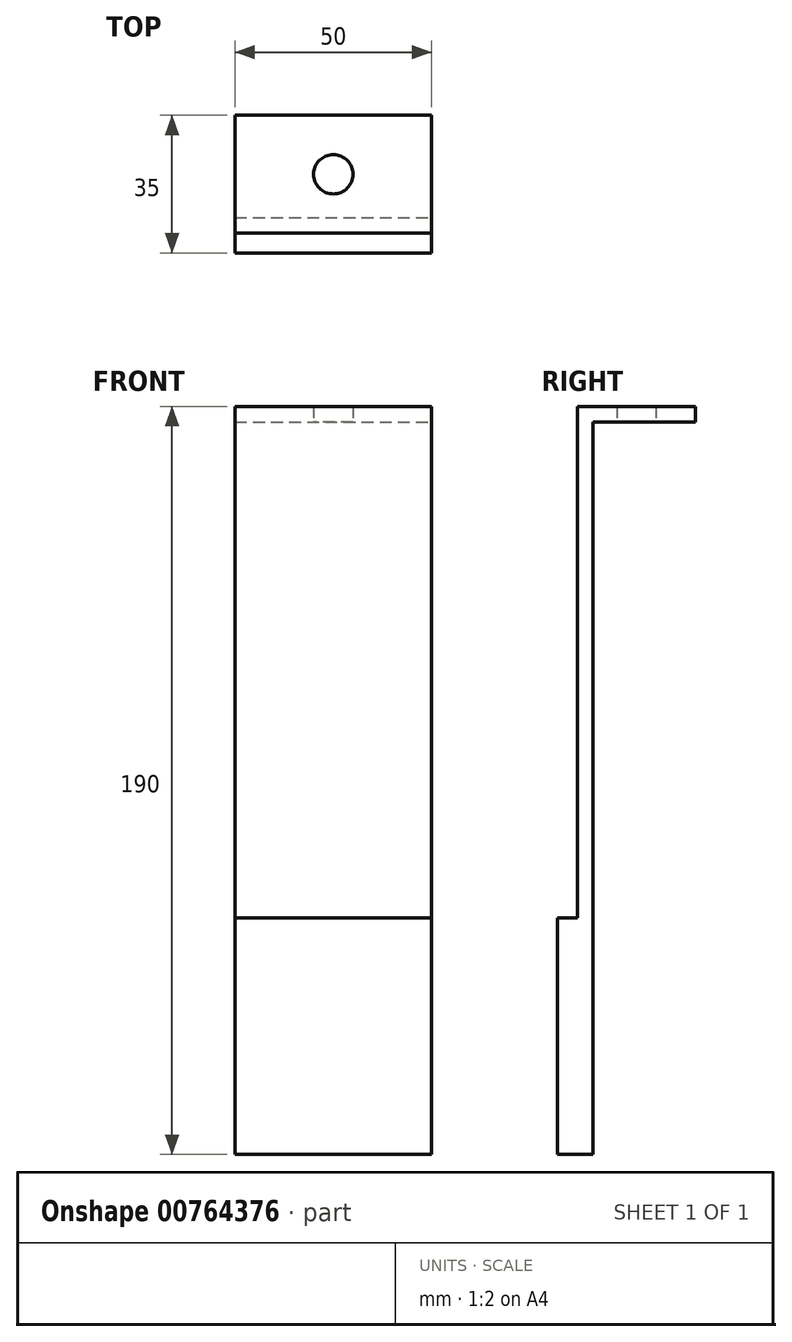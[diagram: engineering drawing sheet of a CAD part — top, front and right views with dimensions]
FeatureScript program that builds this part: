
annotation { "Feature Type Name" : "Feature", "Feature Type Description" : "" }
export const myFeature = defineFeature(function(context is Context, id is Id, definition is map)
    precondition{}
    {
        {
            var Q0;
            Q0=qCreatedBy(makeId("Front.planeOp"),FACE);
            var sketch = newSketch(context, id + "F0", { "sketchPlane" : qUnion([Q0])});
            skLineSegment(sketch, "E0.bottom", {"start": v(-24.82, -95) * mm, "end": v(25.18, -95) * mm});
            skLineSegment(sketch, "E0.top", {"start": v(-24.82, 91) * mm, "end": v(25.18, 91) * mm});
            skLineSegment(sketch, "E0.left", {"start": v(-24.82, -95) * mm, "end": v(-24.82, 91) * mm});
            skLineSegment(sketch, "E0.right", {"start": v(25.18, -95) * mm, "end": v(25.18, 91) * mm});
            skSolve(sketch);
        }
        {
            var Q0;
            Q0=makeQuery(id+"F0.imprint","IMPRINT",FACE,{"disambiguationData":[TD([[makeQuery(id+"F0.imprint","IMPRINT",EDGE,{"derivedFrom":sQuery(id+"F0.wireOp",EDGE,"E0.bottom")}),1.0]])]});
            extrude(context, id + "F1", {"entities" : qUnion([Q0]), "depth" : 4 * mm, "offsetDistance" : 25 * mm, "symmetric" : true});
        }
        {
            var Q0;
            Q0=makeQuery(id+"F1.opExtrude","SWEPT_FACE",FACE,{"disambiguationData":[OSD([sQuery(id+"F0.wireOp",EDGE,"E0.top")])]});
            var sketch = newSketch(context, id + "F2", { "sketchPlane" : qUnion([Q0])});
            skLineSegment(sketch, "E1.bottom", {"start": v(-24.82, -2) * mm, "end": v(25.18, -2) * mm});
            skLineSegment(sketch, "E1.top", {"start": v(-24.82, 28) * mm, "end": v(25.18, 28) * mm});
            skLineSegment(sketch, "E1.left", {"start": v(-24.82, -2) * mm, "end": v(-24.82, 28) * mm});
            skLineSegment(sketch, "E1.right", {"start": v(25.18, -2) * mm, "end": v(25.18, 28) * mm});
            skCircle(sketch, "E2", {"center": v(0.18, 13) * mm, "radius": 5 * mm});
            skSolve(sketch);
        }
        {
            var Q0;
            {var subQ2=sQuery(id+"F2.wireOp",EDGE,"E1.top");Q0=makeQuery(id+"F2.imprint","IMPRINT",FACE,{"disambiguationData":[TD([[makeQuery(id+"F2.imprint","IMPRINT",EDGE,{"derivedFrom":subQ2}),-1.0]])]});}
            var Q1;
            {var subQ0=sQuery(id+"F2.wireOp",EDGE,"E1.bottom");Q1=makeQuery(id+"F2.imprint","IMPRINT",FACE,{"disambiguationData":[TD([[makeQuery(id+"F2.imprint","IMPRINT",EDGE,{"derivedFrom":subQ0}),1.0]])]});}
            extrude(context, id + "F3", {"entities" : qUnion([Q0, Q1]), "operationType" : NewBodyOperationType.ADD, "depth" : 4 * mm, "offsetDistance" : 25 * mm});
        }
        {
            var Q0;
            Q0=makeQuery(id+"F3.boolean.opBoolean","MERGE",FACE,{"derivedFrom":[makeQuery(id+"F1.opExtrude","CAP_FACE",FACE,{"disambiguationData":[OSD([sQuery(id+"F0.wireOp",EDGE,"E0.bottom"),sQuery(id+"F0.wireOp",EDGE,"E0.top"),sQuery(id+"F0.wireOp",EDGE,"E0.left"),sQuery(id+"F0.wireOp",EDGE,"E0.right")])],"isStart":false}),makeQuery(id+"F3.opExtrude","SWEPT_FACE",FACE,{"disambiguationData":[OSD([sQuery(id+"F2.wireOp",EDGE,"E1.bottom")])]})]});
            var sketch = newSketch(context, id + "F4", { "sketchPlane" : qUnion([Q0])});
            skLineSegment(sketch, "E3.bottom", {"start": v(-24.82, -95) * mm, "end": v(25.18, -95) * mm});
            skLineSegment(sketch, "E3.top", {"start": v(-24.82, -35) * mm, "end": v(25.18, -35) * mm});
            skLineSegment(sketch, "E3.left", {"start": v(-24.82, -95) * mm, "end": v(-24.82, -35) * mm});
            skLineSegment(sketch, "E3.right", {"start": v(25.18, -95) * mm, "end": v(25.18, -35) * mm});
            skSolve(sketch);
        }
        {
            var Q0;
            Q0=makeQuery(id+"F4.imprint","IMPRINT",FACE,{"disambiguationData":[TD([[makeQuery(id+"F4.imprint","IMPRINT",EDGE,{"derivedFrom":sQuery(id+"F4.wireOp",EDGE,"E3.bottom")}),1.0]])]});
            extrude(context, id + "F5", {"entities" : qUnion([Q0]), "operationType" : NewBodyOperationType.ADD, "depth" : 5 * mm, "offsetDistance" : 25 * mm});
        }
    });
